# Revit family: RNNB
name_source: partatom
category: 機械設備
units: mm (PartAtom-declared; Revit-internal decimal feet)

## family parameters
OmniClass タイトル = Climate Control (HVAC)
OmniClass 番号 = 23.75.00.00
パーツ タイプ = 標準
ロード時にボイドで切り取り = いいえ
丸型コネクタ寸法 = 直径を使用
作業面ベース = いいえ
共有 = はい
常に垂直 = はい
部屋計算ポイント = いいえ

## types (12) — shared parameters
URL = http://www.3you.co.jp
製造元 = 株式会社サンユー
野縁 = 19  [stored 0.062336 ft]
野縁19(25) = はい
zero-valued in all types: 既定の高さ

## per-type parameters (varying)
| type | t | 野縁受け幅 |
| C38型 | 0.8  [stored 0.00262467 ft] | 38  [stored 0.124672 ft] |
| C40型 | 0.8  [stored 0.00262467 ft] | 40  [stored 0.131234 ft] |
| C45型 | 0.8  [stored 0.00262467 ft] | 45  [stored 0.147638 ft] |
| C50型 | 0.8  [stored 0.00262467 ft] | 50  [stored 0.164042 ft] |
| C65型 | 0.8  [stored 0.00262467 ft] | 65  [stored 0.213255 ft] |
| C65型　t1.6 | 1.6  [stored 0.00524934 ft] | 65  [stored 0.213255 ft] |
| C75型　t1.6 | 1.6  [stored 0.00524934 ft] | 75 |
| C75型 | 0.8  [stored 0.00262467 ft] | 75 |
| C90型 | 0.8  [stored 0.00262467 ft] | 90  [stored 0.295276 ft] |
| C90型　t1.6 | 1.6  [stored 0.00524934 ft] | 90  [stored 0.295276 ft] |
| C100型　t1.6 | 1.6  [stored 0.00524934 ft] | 100  [stored 0.328084 ft] |
| C100型 | 0.8  [stored 0.00262467 ft] | 100  [stored 0.328084 ft] |

note: [stored X ft] marks values corroborated as IEEE doubles in the binary element streams (Revit-internal decimal feet)
